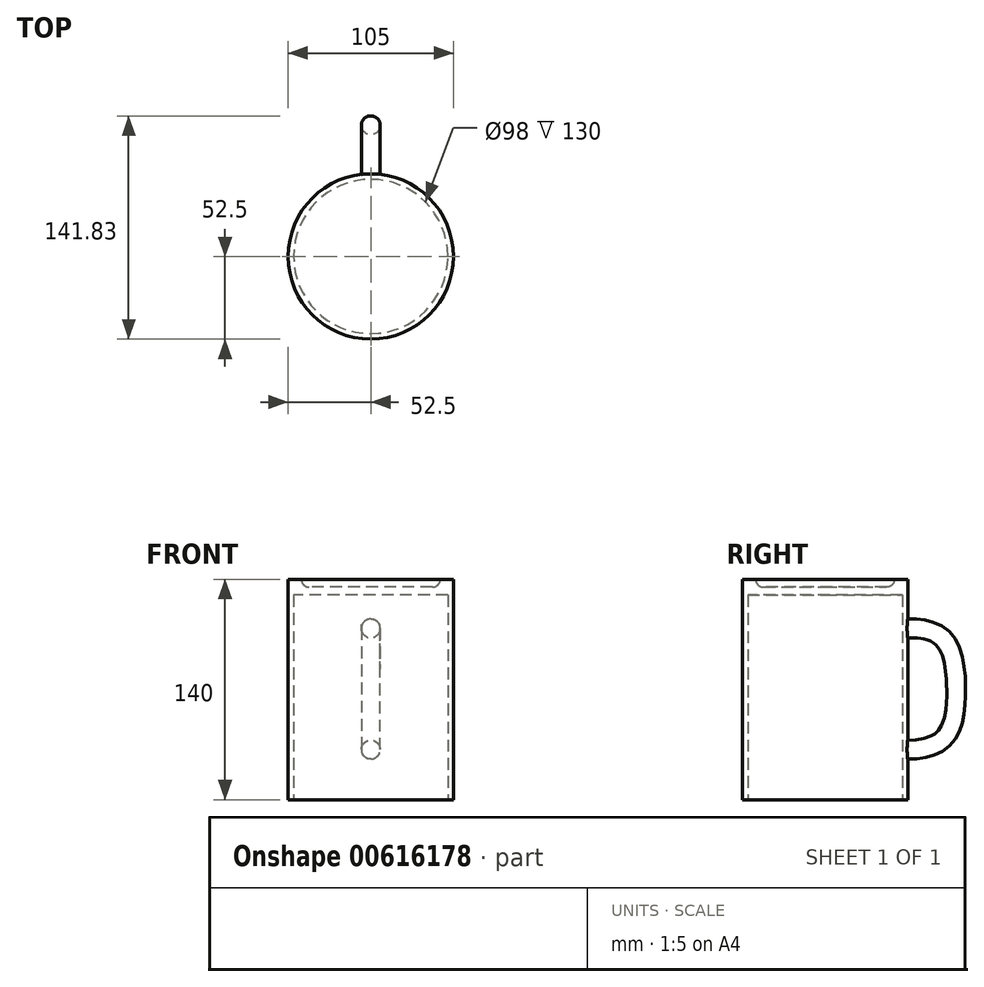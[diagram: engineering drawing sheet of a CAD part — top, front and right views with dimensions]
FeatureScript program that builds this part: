
annotation { "Feature Type Name" : "Feature", "Feature Type Description" : "" }
export const myFeature = defineFeature(function(context is Context, id is Id, definition is map)
    precondition{}
    {
        {
            var Q0;
            Q0=qCreatedBy(makeId("Top.planeOp"),FACE);
            var sketch = newSketch(context, id + "F0", { "sketchPlane" : qUnion([Q0])});
            skCircle(sketch, "E0", {"center": v(0, 0) * mm, "radius": 52.5 * mm});
            skSolve(sketch);
        }
        {
            var Q0;
            Q0 = qSketchRegion(id + "F0", true);
            extrude(context, id + "F1", {"entities" : qUnion([Q0]), "depth" : 140 * mm, "offsetDistance" : 25 * mm});
        }
        {
            var Q0;
            Q0=qCreatedBy(makeId("Right.planeOp"),FACE);
            var sketch = newSketch(context, id + "F2", { "sketchPlane" : qUnion([Q0])});
            skFitSpline(sketch, "E1", {"points": [v(48.7, 32.3) * mm, v(75.04, 38.98) * mm, v(82.98, 66.99) * mm, v(75.04, 101.69) * mm, v(49.96, 108.38) * mm], "startDerivative": vector(130.34, -10.43) * mm, "endDerivative": vector(-124.42, -5.4) * mm});
            skSolve(sketch);
        }
        {
            var Q0;
            Q0=qCreatedBy(makeId("Front.planeOp"),FACE);
            cPlane(context, id + "F3", {"entities" : qUnion([Q0]), "cplaneType" : CPlaneType.OFFSET, "offset" : 49.9 * mm, "oppositeDirection" : true, "width" : 150 * mm, "height" : 150 * mm});
        }
        {
            var Q0;
            Q0=qCreatedBy(id+"F3.planeOp",FACE);
            var sketch = newSketch(context, id + "F4", { "sketchPlane" : qUnion([Q0])});
            skCircle(sketch, "E2", {"center": v(0, 31.87) * mm, "radius": 6 * mm});
            skSolve(sketch);
        }
        {
            var Q0;
            Q0 = qSketchRegion(id + "F4", true);
            var Q1;
            Q1 = qConstructionFilter(qBodyType(qCreatedBy(id + "F2" ,EDGE), BodyType.WIRE), ConstructionObject.NO);
            sweep(context, id + "F5", {"operationType" : NewBodyOperationType.ADD, "profiles" : qUnion([Q0]), "path" : qUnion([Q1])});
        }
        {
            var Q0;
            Q0=qCreatedBy(makeId("Top.planeOp"),FACE);
            var sketch = newSketch(context, id + "F6", { "sketchPlane" : qUnion([Q0])});
            skCircle(sketch, "E3", {"center": v(0, 0) * mm, "radius": 49 * mm});
            skSolve(sketch);
        }
        {
            var Q0;
            Q0 = qSketchRegion(id + "F6", true);
            extrude(context, id + "F7", {"entities" : qUnion([Q0]), "operationType" : NewBodyOperationType.REMOVE, "depth" : 130 * mm, "offsetDistance" : 25 * mm});
        }
        {
            var Q0;
            Q0=makeQuery(id+"F1.opExtrude","CAP_FACE",FACE,{"disambiguationData":[OSD([sQuery(id+"F0.wireOp",EDGE,"E0")])],"isStart":false});
            var sketch = newSketch(context, id + "F8", { "sketchPlane" : qUnion([Q0])});
            skCircle(sketch, "E4", {"center": v(0, 0) * mm, "radius": 44.1 * mm});
            skSolve(sketch);
        }
        {
            var Q0;
            Q0 = qSketchRegion(id + "F8", true);
            extrude(context, id + "F9", {"entities" : qUnion([Q0]), "operationType" : NewBodyOperationType.REMOVE, "oppositeDirection" : true, "depth" : 5 * mm, "offsetDistance" : 25 * mm});
        }
        {
            var Q0;
            Q0=makeQuery(id+"F9.boolean.opBoolean","COPY",EDGE,{"derivedFrom":makeQuery(id+"F9.opExtrude","CAP_EDGE",EDGE,{"disambiguationData":[OSD([sQuery(id+"F8.wireOp",EDGE,"E4")])],"isStart":false})});
            fillet(context, id + "F10", {"entities" : qUnion([Q0]), "radius" : 5 * mm, "tangentPropagation" : true, "allowEdgeOverflow" : false});
        }
        {
            var Q0;
            Q0=makeQuery(id+"F10.opFillet","BLEND_EDGE",EDGE,{"blendedFrom":[makeQuery(id+"F9.boolean.opBoolean","COPY",EDGE,{"derivedFrom":makeQuery(id+"F9.opExtrude","CAP_EDGE",EDGE,{"disambiguationData":[OSD([sQuery(id+"F8.wireOp",EDGE,"E4")])],"isStart":false})}),makeQuery(id+"F1.opExtrude","CAP_FACE",FACE,{"disambiguationData":[OSD([sQuery(id+"F0.wireOp",EDGE,"E0")])],"isStart":false})],"blendedInto":[makeQuery(id+"F1.opExtrude","CAP_FACE",FACE,{"disambiguationData":[OSD([sQuery(id+"F0.wireOp",EDGE,"E0")])],"isStart":false})]});
            fillet(context, id + "F11", {"entities" : qUnion([Q0]), "radius" : 0.5 * mm, "tangentPropagation" : true, "allowEdgeOverflow" : false});
        }
    });
